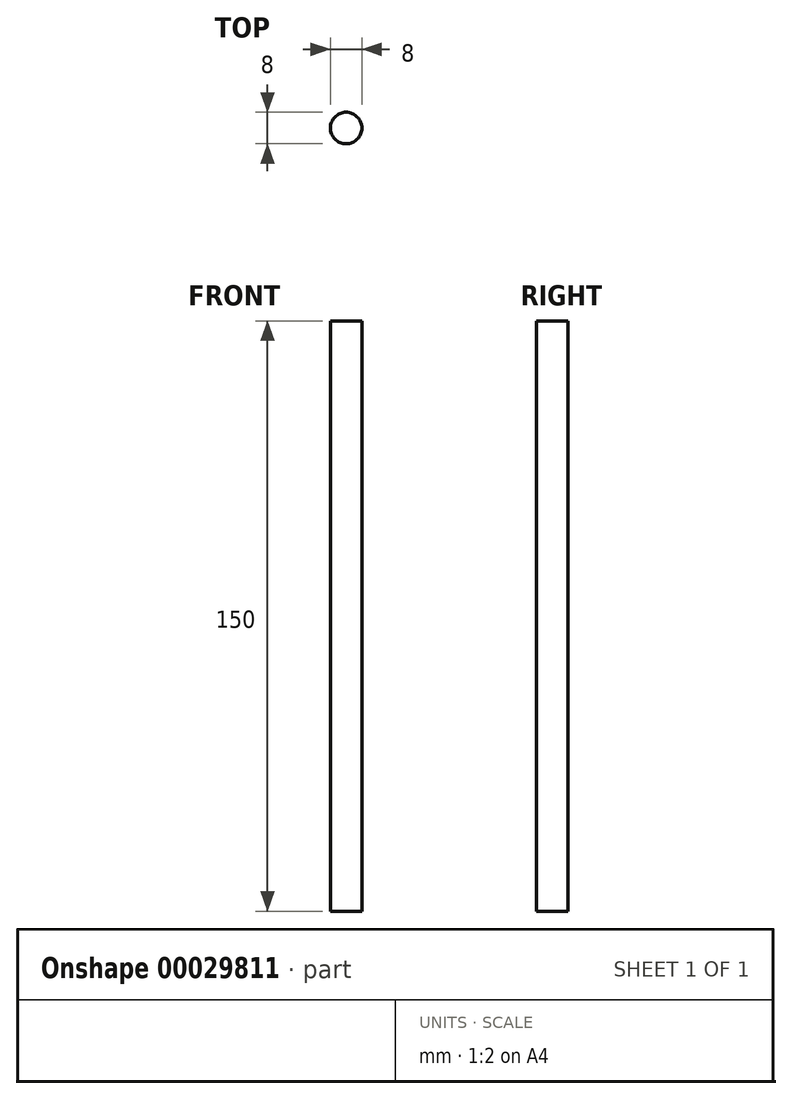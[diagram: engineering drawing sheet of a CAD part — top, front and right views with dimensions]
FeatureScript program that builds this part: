
annotation { "Feature Type Name" : "Feature", "Feature Type Description" : "" }
export const myFeature = defineFeature(function(context is Context, id is Id, definition is map)
    precondition{}
    {
        {
            var Q0;
            Q0=qCreatedBy(makeId("Top.planeOp"),FACE);
            var sketch = newSketch(context, id + "F0", { "sketchPlane" : qUnion([Q0])});
            skCircle(sketch, "E0", {"center": v(0, 0) * mm, "radius": 4 * mm});
            skSolve(sketch);
        }
        {
            var Q0;
            Q0 = qSketchRegion(id + "F0", true);
            extrude(context, id + "F1", {"entities" : qUnion([Q0]), "endBound" : BoundingType.SYMMETRIC, "depth" : 150 * mm});
        }
    });
